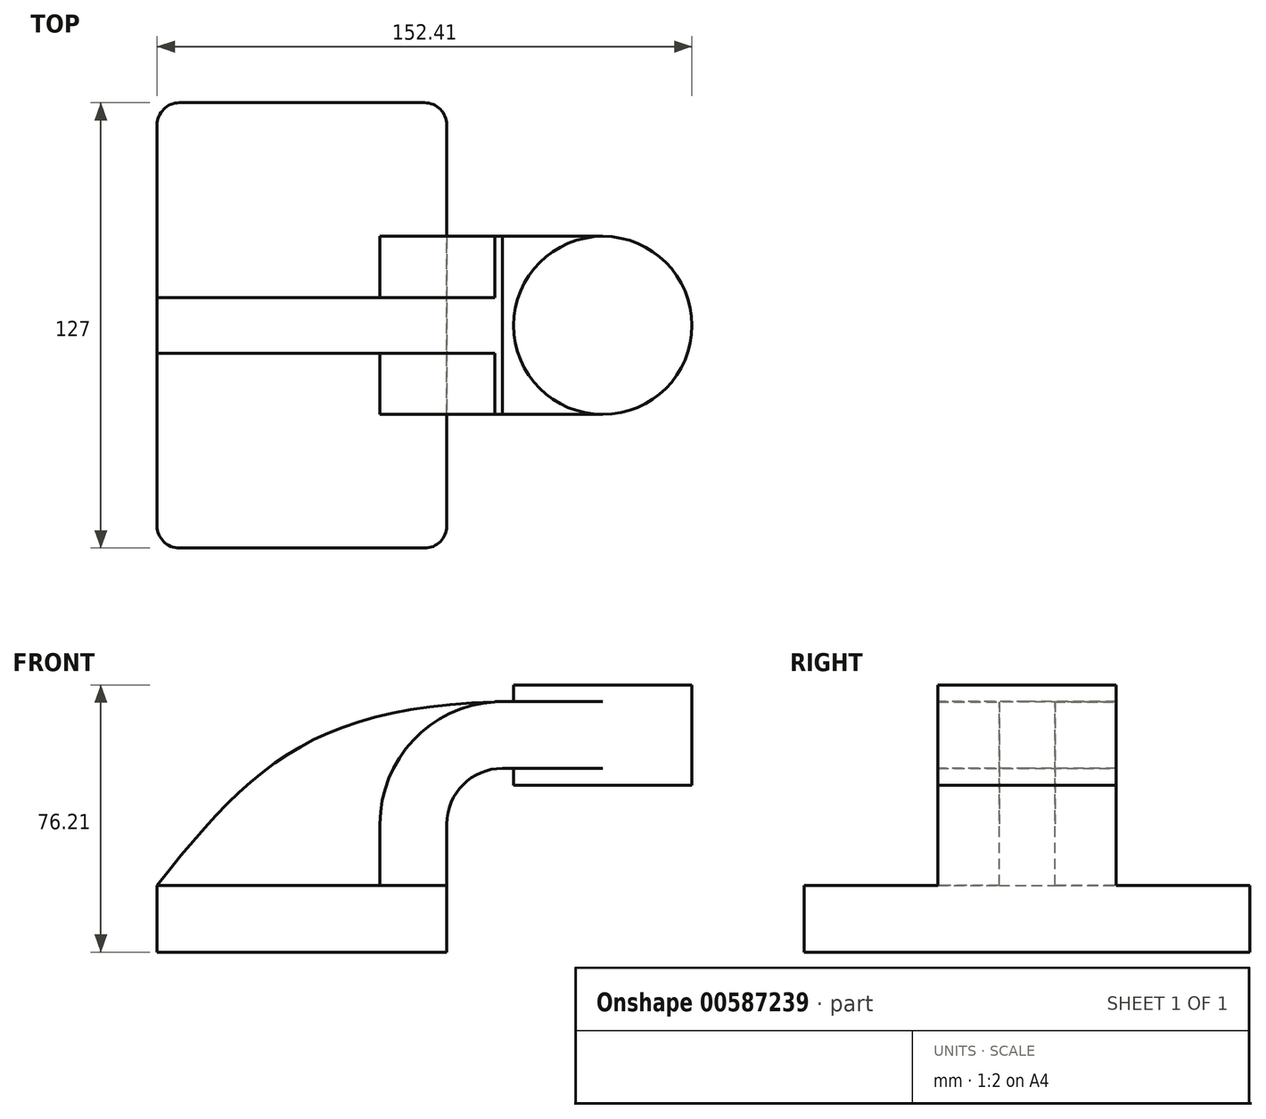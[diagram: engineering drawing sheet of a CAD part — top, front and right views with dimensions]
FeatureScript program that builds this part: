
annotation { "Feature Type Name" : "Feature", "Feature Type Description" : "" }
export const myFeature = defineFeature(function(context is Context, id is Id, definition is map)
    precondition{}
    {
        {
            var Q0;
            Q0=qCreatedBy(makeId("Front.planeOp"),FACE);
            var sketch = newSketch(context, id + "F0", { "sketchPlane" : qUnion([Q0])});
            skLineSegment(sketch, "E0.bottom", {"start": v(-41.28, 9.52) * mm, "end": v(41.28, 9.53) * mm});
            skLineSegment(sketch, "E0.top", {"start": v(-41.28, -9.53) * mm, "end": v(41.28, -9.53) * mm});
            skLineSegment(sketch, "E0.left", {"start": v(-41.28, 9.52) * mm, "end": v(-41.27, -9.53) * mm});
            skLineSegment(sketch, "E0.right", {"start": v(41.28, 9.53) * mm, "end": v(41.28, -9.52) * mm});
            skPoint(sketch, "E0.middle", {"position": v(0, 0) * mm});
            skLineSegment(sketch, "E1.bottom", {"start": v(60.32, 66.68) * mm, "end": v(111.12, 66.68) * mm});
            skLineSegment(sketch, "E1.top", {"start": v(60.32, 38.1) * mm, "end": v(111.12, 38.1) * mm});
            skLineSegment(sketch, "E1.left", {"start": v(60.32, 66.68) * mm, "end": v(60.32, 38.1) * mm});
            skLineSegment(sketch, "E1.right", {"start": v(111.12, 66.68) * mm, "end": v(111.12, 38.1) * mm});
            skPoint(sketch, "E1.middle", {"position": v(85.72, 52.39) * mm});
            skLineSegment(sketch, "E2", {"start": v(41.27, 9.53) * mm, "end": v(41.27, 27) * mm});
            skArc(sketch, "E3", {"start": v(41.27, 27) * mm, "mid": v(45.92, 38.23) * mm, "end": v(57.15, 42.88) * mm});
            skLineSegment(sketch, "E4", {"start": v(57.15, 42.88) * mm, "end": v(85.72, 42.88) * mm});
            skLineSegment(sketch, "E5.0", {"start": v(57.15, 61.93) * mm, "end": v(85.72, 61.93) * mm});
            skArc(sketch, "E5.1", {"start": v(22.22, 27) * mm, "mid": v(32.45, 51.7) * mm, "end": v(57.15, 61.93) * mm});
            skLineSegment(sketch, "E5.2", {"start": v(22.22, 9.53) * mm, "end": v(22.22, 27) * mm});
            skLineSegment(sketch, "E6", {"start": v(85.72, 38.1) * mm, "end": v(85.72, 66.68) * mm});
            skFitSpline(sketch, "E7", {"points": [v(-41.28, 9.52) * mm, v(57.15, 61.93) * mm], "startDerivative": vector(82.32, 105.03) * mm, "endDerivative": vector(159.51, 4.42) * mm});
            skSolve(sketch);
        }
        {
            var Q0;
            Q0=makeQuery(id+"F0.imprint","IMPRINT",FACE,{"disambiguationData":[TD([[makeQuery(id+"F0.imprint","IMPRINT",EDGE,{"derivedFrom":sQuery(id+"F0.wireOp",EDGE,"E0.top")}),1.0]])]});
            extrude(context, id + "F1", {"entities" : qUnion([Q0]), "endBound" : BoundingType.SYMMETRIC, "oppositeDirection" : true, "depth" : 127 * mm, "offsetDistance" : 25.4 * mm});
        }
        {
            var Q0;
            {var subQ1=sQuery(id+"F0.wireOp",EDGE,"E2");Q0=makeQuery(id+"F0.imprint","IMPRINT",FACE,{"disambiguationData":[TD([[makeQuery(id+"F0.imprint","IMPRINT",EDGE,{"derivedFrom":subQ1}),1.0]])]});}
            extrude(context, id + "F2", {"entities" : qUnion([Q0]), "operationType" : NewBodyOperationType.ADD, "endBound" : BoundingType.SYMMETRIC, "depth" : 50.8 * mm, "offsetDistance" : 25.4 * mm});
        }
        {
            var Q0;
            {var subQ3=sQuery(id+"F0.wireOp",EDGE,"E5.2");Q0=makeQuery(id+"F0.imprint","IMPRINT",FACE,{"disambiguationData":[TD([[makeQuery(id+"F0.imprint","IMPRINT",EDGE,{"derivedFrom":subQ3}),1.0]])]});}
            extrude(context, id + "F3", {"entities" : qUnion([Q0]), "operationType" : NewBodyOperationType.ADD, "endBound" : BoundingType.SYMMETRIC, "depth" : 15.88 * mm, "offsetDistance" : 25.4 * mm});
        }
        {
            var Q0;
            {var subQ0=sQuery(id+"F0.wireOp",EDGE,"E5.0");var subQ1=sQuery(id+"F0.wireOp",EDGE,"E1.left");var subQ2=makeQuery(id+"F0.imprint","INTERSECT",VERTEX,{"derivedFrom":[subQ1,subQ0]});Q0=makeQuery(id+"F0.imprint","IMPRINT",FACE,{"disambiguationData":[TD([[makeQuery(id+"F0.imprint","IMPRINT",EDGE,{"disambiguationData":[TD([[subQ2,-1.0]])],"derivedFrom":subQ1}),1.0]])]});}
            extrude(context, id + "F4", {"entities" : qUnion([Q0]), "operationType" : NewBodyOperationType.ADD, "endBound" : BoundingType.SYMMETRIC, "depth" : 50.8 * mm, "offsetDistance" : 25.4 * mm});
        }
        {
            var Q0;
            {var subQ4=sQuery(id+"F0.wireOp",EDGE,"E1.right");Q0=makeQuery(id+"F0.imprint","IMPRINT",FACE,{"disambiguationData":[TD([[makeQuery(id+"F0.imprint","IMPRINT",EDGE,{"derivedFrom":subQ4}),-1.0]])]});}
            var Q1;
            Q1=sQuery(id+"F0.wireOp",EDGE,"E6");
            revolve(context, id + "F5", {"operationType" : NewBodyOperationType.ADD, "entities" : qUnion([Q0]), "axis" : qUnion([Q1]), "revolveType" : RevolveType.FULL});
        }
        {
            var Q0;
            Q0=makeQuery(id+"F1.opExtrude","CAP_EDGE",EDGE,{"disambiguationData":[OSD([sQuery(id+"F0.wireOp",EDGE,"E0.right")])],"isStart":true});
            var Q1;
            Q1=makeQuery(id+"F1.opExtrude","CAP_EDGE",EDGE,{"disambiguationData":[OSD([sQuery(id+"F0.wireOp",EDGE,"E0.left")])],"isStart":true});
            var Q2;
            Q2=makeQuery(id+"F1.opExtrude","CAP_EDGE",EDGE,{"disambiguationData":[OSD([sQuery(id+"F0.wireOp",EDGE,"E0.right")])],"isStart":false});
            var Q3;
            Q3=makeQuery(id+"F1.opExtrude","CAP_EDGE",EDGE,{"disambiguationData":[OSD([sQuery(id+"F0.wireOp",EDGE,"E0.left")])],"isStart":false});
            fillet(context, id + "F6", {"entities" : qUnion([Q0, Q1, Q2, Q3]), "radius" : 6.35 * mm, "tangentPropagation" : true, "allowEdgeOverflow" : false});
        }
    });
